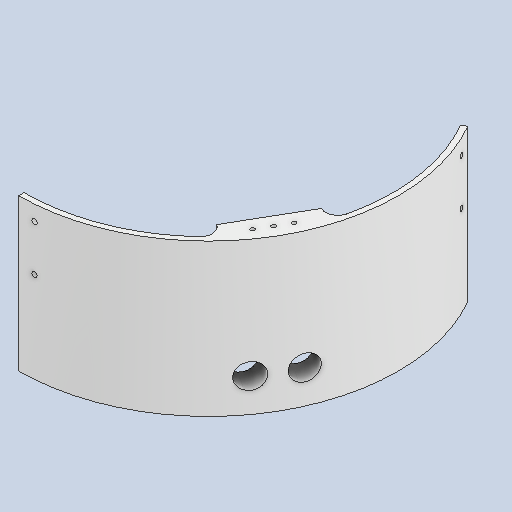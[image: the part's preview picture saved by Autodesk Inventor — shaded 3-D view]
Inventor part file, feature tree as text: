
AUTODESK INVENTOR PART (.ipt)
format: ipt  version: 2023 (Build 270158000, 158)  size: 399,360 bytes
history: native  units: mm
features: sketch x20, extrude x13, hole x7, other x1, fillet x1
ambient origin geometry x8: Origin, YZ Plane, XZ Plane, XY Plane, X Axis, Y Axis, Z Axis, Center Point
bodies: Body1 (feature_tree)
feature tree (42):
  other  "ソリッド1"
  extrude  "押し出し1"  Depth=250.0mm
  extrude  "押し出し2"  Depth=375.0mm TaperAngle=0.0deg
  hole  "穴1"  [1 undecoded]
  hole  "穴2"  [1 undecoded]
  extrude  "押し出し3"  Depth=30.0mm TaperAngle=360.0deg
  extrude  "押し出し4"  Depth=10.0mm
  hole  "穴4"  [1 undecoded]
  hole  "穴5"  [1 undecoded]
  extrude  "押し出し6"  Depth=330.0mm TaperAngle=0.0deg
  extrude  "押し出し7"  Depth=118.0mm
  extrude  "押し出し8"  Depth=30.0mm TaperAngle=360.0deg
  extrude  "押し出し9"  Depth=330.0mm TaperAngle=0.0deg
  extrude  "押し出し11"  Depth=30.0mm
  extrude  "押し出し12"  Depth=30.0mm
  extrude  "押し出し13"  Depth=243.0mm
  extrude  "押し出し14"  Depth=330.0mm TaperAngle=0.0deg
  fillet  "フィレット1"  Radius=125.0mm
  extrude  "押し出し15"  TaperAngle=120.0deg  [1 undecoded]
  hole  "穴6"  [1 undecoded]
  hole  "穴7"  [1 undecoded]
  hole  "穴8"  [1 undecoded]
  sketch  "スケッチ1"
  sketch  "スケッチ2"
  sketch  "スケッチ3"
  sketch  "スケッチ4"
  sketch  "スケッチ5"
  sketch  "スケッチ6"
  sketch  "スケッチ8"
  sketch  "スケッチ11"
  sketch  "スケッチ12"
  sketch  "スケッチ13"
  sketch  "スケッチ14"
  sketch  "スケッチ15"
  sketch  "スケッチ17"
  sketch  "スケッチ18"
  sketch  "スケッチ19"
  sketch  "スケッチ20"
  sketch  "スケッチ21"
  sketch  "スケッチ22"
  sketch  "スケッチ23"
  sketch  "スケッチ24"
note: 8 required parameter values undecoded (feature->parameter linkage not recoverable at this tier; creation-order binding heuristic only, values carry confidence <= 0.55)
